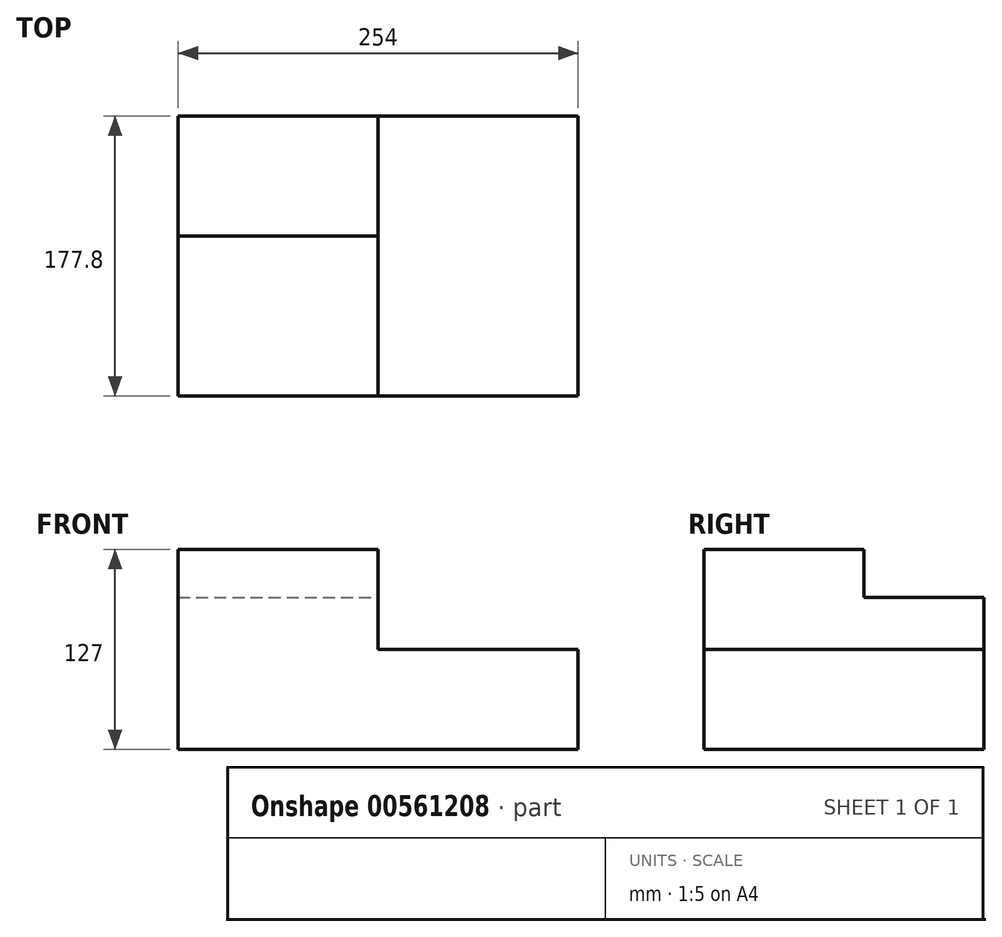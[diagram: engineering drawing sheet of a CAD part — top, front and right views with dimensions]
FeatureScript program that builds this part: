
annotation { "Feature Type Name" : "Feature", "Feature Type Description" : "" }
export const myFeature = defineFeature(function(context is Context, id is Id, definition is map)
    precondition{}
    {
        {
            var Q0;
            Q0=qCreatedBy(makeId("Front.planeOp"),FACE);
            var sketch = newSketch(context, id + "F0", { "sketchPlane" : qUnion([Q0])});
            skLineSegment(sketch, "E0", {"start": v(0, 0) * mm, "end": v(-254, 0) * mm});
            skLineSegment(sketch, "E1", {"start": v(-254, 0) * mm, "end": v(-254, 96.52) * mm});
            skLineSegment(sketch, "E2", {"start": v(-254, 96.52) * mm, "end": v(-127, 96.52) * mm});
            skLineSegment(sketch, "E3", {"start": v(-127, 96.52) * mm, "end": v(-127, 63.5) * mm});
            skLineSegment(sketch, "E4", {"start": v(-127, 63.5) * mm, "end": v(0, 63.5) * mm});
            skLineSegment(sketch, "E5", {"start": v(0, 63.5) * mm, "end": v(0, 0) * mm});
            skSolve(sketch);
        }
        {
            var Q0;
            Q0 = qSketchRegion(id + "F0", true);
            extrude(context, id + "F1", {"entities" : qUnion([Q0]), "depth" : 177.8 * mm, "offsetDistance" : 25.4 * mm});
        }
        {
            var Q0;
            Q0=makeQuery(id+"F1.opExtrude","SWEPT_FACE",FACE,{"disambiguationData":[OSD([sQuery(id+"F0.wireOp",EDGE,"E2")])]});
            var sketch = newSketch(context, id + "F2", { "sketchPlane" : qUnion([Q0])});
            skLineSegment(sketch, "E6", {"start": v(-254, -177.8) * mm, "end": v(-254, -76.2) * mm});
            skLineSegment(sketch, "E7", {"start": v(-254, -76.2) * mm, "end": v(-127, -76.2) * mm});
            skLineSegment(sketch, "E8", {"start": v(-127, -76.2) * mm, "end": v(-127, -177.8) * mm});
            skLineSegment(sketch, "E9", {"start": v(-127, -177.8) * mm, "end": v(-254, -177.8) * mm});
            skSolve(sketch);
        }
        {
            var Q0;
            Q0=makeQuery(id+"F2.imprint","IMPRINT",FACE,{"disambiguationData":[TD([[makeQuery(id+"F2.imprint","IMPRINT",EDGE,{"derivedFrom":sQuery(id+"F2.wireOp",EDGE,"E6")}),-1.0]])]});
            extrude(context, id + "F3", {"entities" : qUnion([Q0]), "operationType" : NewBodyOperationType.ADD, "depth" : 30.48 * mm, "offsetDistance" : 25.4 * mm});
        }
    });
